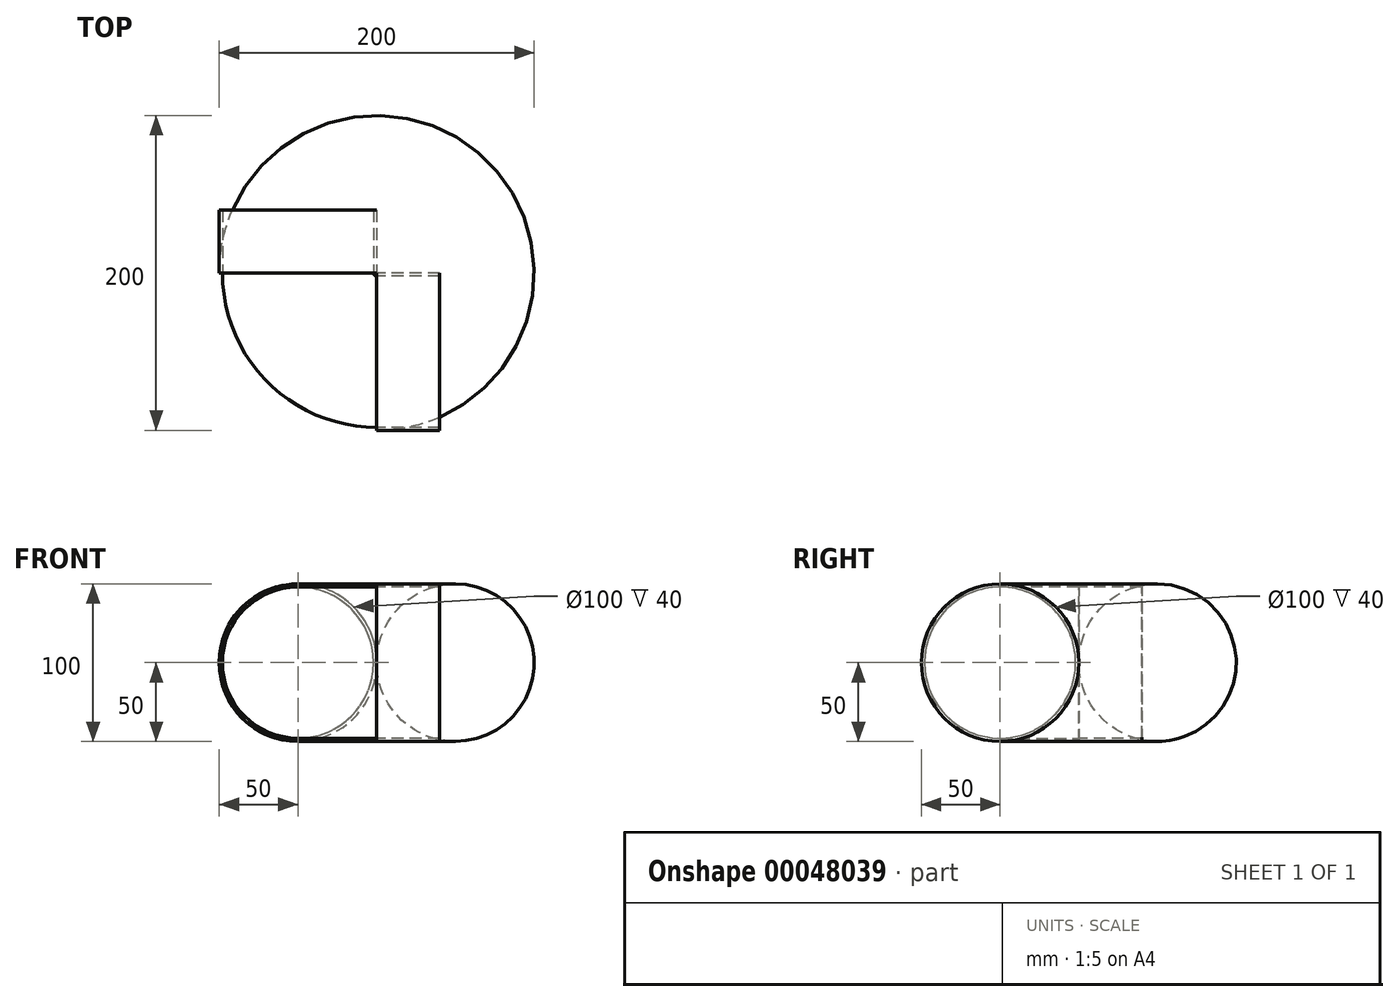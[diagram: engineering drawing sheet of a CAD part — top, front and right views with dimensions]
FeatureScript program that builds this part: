
annotation { "Feature Type Name" : "Feature", "Feature Type Description" : "" }
export const myFeature = defineFeature(function(context is Context, id is Id, definition is map)
    precondition{}
    {
        {
            var Q0;
            Q0=qCreatedBy(makeId("Front.planeOp"),FACE);
            var sketch = newSketch(context, id + "F0", { "sketchPlane" : qUnion([Q0])});
            skCircle(sketch, "E0", {"center": v(0, 0) * mm, "radius": 50 * mm});
            skCircle(sketch, "E1.0", {"center": v(0, 0) * mm, "radius": 48 * mm});
            skLineSegment(sketch, "E2", {"start": v(50, 0) * mm, "end": v(50, 68.99) * mm, "construction": true});
            skSolve(sketch);
        }
        {
            var Q0;
            Q0 = qSketchRegion(id + "F0", true);
            var Q1;
            Q1=sQuery(id+"F0.wireOp",EDGE,"E2");
            revolve(context, id + "F1", {"entities" : qUnion([Q0]), "axis" : qUnion([Q1]), "revolveType" : RevolveType.ONE_DIRECTION, "angle" : 90 * degree});
        }
        {
            var Q0;
            Q0=makeQuery(id+"F1.opRevolve","CAP_FACE",FACE,{"disambiguationData":[OSD([sQuery(id+"F0.wireOp",EDGE,"E0"),sQuery(id+"F0.wireOp",EDGE,"E1.0")])],"isStart":false});
            var sketch = newSketch(context, id + "F2", { "sketchPlane" : qUnion([Q0])});
            skCircle(sketch, "E3.0", {"center": v(-50, 0) * mm, "radius": 48 * mm});
            skCircle(sketch, "E3.1", {"center": v(-50, 0) * mm, "radius": 50 * mm});
            skSolve(sketch);
        }
        {
            var Q0;
            Q0 = qSketchRegion(id + "F2", true);
            extrude(context, id + "F3", {"entities" : qUnion([Q0]), "operationType" : NewBodyOperationType.ADD, "depth" : 40 * mm});
        }
        {
            var Q0;
            Q0=makeQuery(id+"F1.opRevolve","CAP_FACE",FACE,{"disambiguationData":[OSD([sQuery(id+"F0.wireOp",EDGE,"E0"),sQuery(id+"F0.wireOp",EDGE,"E1.0")])],"isStart":true});
            var sketch = newSketch(context, id + "F4", { "sketchPlane" : qUnion([Q0])});
            skCircle(sketch, "E4.0", {"center": v(0, 0) * mm, "radius": 48 * mm});
            skCircle(sketch, "E4.1", {"center": v(0, 0) * mm, "radius": 50 * mm});
            skSolve(sketch);
        }
        {
            var Q0;
            Q0 = qSketchRegion(id + "F4", true);
            extrude(context, id + "F5", {"entities" : qUnion([Q0]), "operationType" : NewBodyOperationType.ADD, "depth" : 40 * mm});
        }
    });
